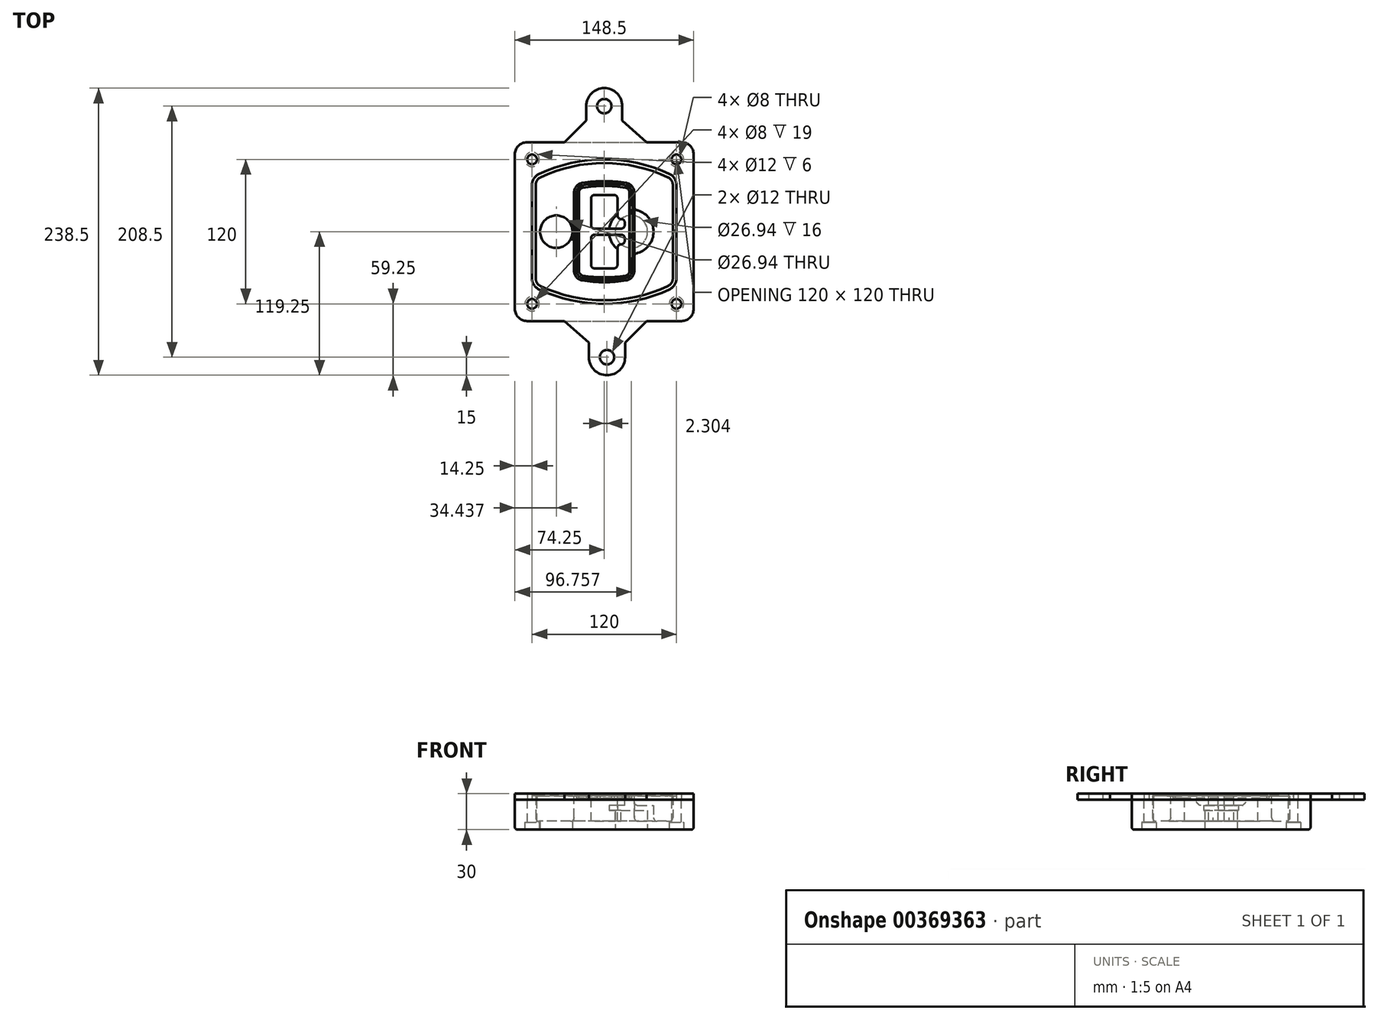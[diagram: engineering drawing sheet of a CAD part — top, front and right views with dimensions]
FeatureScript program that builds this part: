
annotation { "Feature Type Name" : "Feature", "Feature Type Description" : "" }
export const myFeature = defineFeature(function(context is Context, id is Id, definition is map)
    precondition{}
    {
        {
            var Q0;
            Q0=qCreatedBy(makeId("Top.planeOp"),FACE);
            var sketch = newSketch(context, id + "F0", { "sketchPlane" : qUnion([Q0])});
            skPoint(sketch, "E0.rect.middle", {"position": v(0, 0) * mm});
            skLineSegment(sketch, "E1.bottom", {"start": v(-64.25, -74.25) * mm, "end": v(64.25, -74.25) * mm});
            skLineSegment(sketch, "E1.top", {"start": v(-64.25, 74.25) * mm, "end": v(64.25, 74.25) * mm});
            skLineSegment(sketch, "E1.left", {"start": v(-74.25, -64.25) * mm, "end": v(-74.25, 64.25) * mm});
            skLineSegment(sketch, "E1.right", {"start": v(74.25, -64.25) * mm, "end": v(74.25, 64.25) * mm});
            skLineSegment(sketch, "E2", {"start": v(-74.25, 74.25) * mm, "end": v(74.25, -74.25) * mm, "construction": true});
            skLineSegment(sketch, "E3", {"start": v(74.25, 74.25) * mm, "end": v(-74.25, -74.25) * mm, "construction": true});
            skCircle(sketch, "E4", {"center": v(-60, 60) * mm, "radius": 4 * mm});
            skCircle(sketch, "E5", {"center": v(60, 60) * mm, "radius": 4 * mm});
            skCircle(sketch, "E6", {"center": v(60, -60) * mm, "radius": 4 * mm});
            skCircle(sketch, "E7", {"center": v(-60, -60) * mm, "radius": 4 * mm});
            skLineSegment(sketch, "E8", {"start": v(-60, 60) * mm, "end": v(60, 60) * mm, "construction": true});
            skLineSegment(sketch, "E9", {"start": v(60, 60) * mm, "end": v(60, -60) * mm, "construction": true});
            skLineSegment(sketch, "E10", {"start": v(60, -60) * mm, "end": v(-60, -60) * mm, "construction": true});
            skLineSegment(sketch, "E11", {"start": v(-60, -60) * mm, "end": v(-60, 60) * mm, "construction": true});
            skLineSegment(sketch, "E12", {"start": v(-60, 38.83) * mm, "end": v(-60, -38.83) * mm});
            skLineSegment(sketch, "E13", {"start": v(60, 38.83) * mm, "end": v(60, -38.83) * mm});
            skArc(sketch, "E14", {"start": v(54.26, 47.88) * mm, "mid": v(0, 60) * mm, "end": v(-54.26, 47.88) * mm});
            skArc(sketch, "E15", {"start": v(-54.26, -47.88) * mm, "mid": v(0, -60) * mm, "end": v(54.26, -47.88) * mm});
            skLineSegment(sketch, "E16", {"start": v(-60, 0) * mm, "end": v(60, 0) * mm, "construction": true});
            skPoint(sketch, "E17.visualSharp", {"position": v(-60, -45) * mm});
            skArc(sketch, "E17.filletArc", {"start": v(-60, -38.83) * mm, "mid": v(-58.44, -44.2) * mm, "end": v(-54.26, -47.88) * mm});
            skPoint(sketch, "E18.visualSharp", {"position": v(-60, 45) * mm});
            skArc(sketch, "E18.filletArc", {"start": v(-54.26, 47.88) * mm, "mid": v(-58.44, 44.2) * mm, "end": v(-60, 38.83) * mm});
            skPoint(sketch, "E19.visualSharp", {"position": v(60, 45) * mm});
            skArc(sketch, "E19.filletArc", {"start": v(60, 38.83) * mm, "mid": v(58.44, 44.2) * mm, "end": v(54.26, 47.88) * mm});
            skPoint(sketch, "E20.visualSharp", {"position": v(60, -45) * mm});
            skArc(sketch, "E20.filletArc", {"start": v(54.26, -47.88) * mm, "mid": v(58.44, -44.2) * mm, "end": v(60, -38.83) * mm});
            skPoint(sketch, "E21.visualSharp", {"position": v(-74.25, 74.25) * mm});
            skArc(sketch, "E21.filletArc", {"start": v(-64.25, 74.25) * mm, "mid": v(-71.32, 71.32) * mm, "end": v(-74.25, 64.25) * mm});
            skPoint(sketch, "E22.visualSharp", {"position": v(74.25, 74.25) * mm});
            skArc(sketch, "E22.filletArc", {"start": v(74.25, 64.25) * mm, "mid": v(71.32, 71.32) * mm, "end": v(64.25, 74.25) * mm});
            skPoint(sketch, "E23.visualSharp", {"position": v(74.25, -74.25) * mm});
            skArc(sketch, "E23.filletArc", {"start": v(64.25, -74.25) * mm, "mid": v(71.32, -71.32) * mm, "end": v(74.25, -64.25) * mm});
            skPoint(sketch, "E24.visualSharp", {"position": v(-74.25, -74.25) * mm});
            skArc(sketch, "E24.filletArc", {"start": v(-74.25, -64.25) * mm, "mid": v(-71.32, -71.32) * mm, "end": v(-64.25, -74.25) * mm});
            skArc(sketch, "E25.0", {"start": v(57, 38.83) * mm, "mid": v(55.9, 42.58) * mm, "end": v(52.98, 45.17) * mm});
            skLineSegment(sketch, "E25.1", {"start": v(57, 38.83) * mm, "end": v(57, -38.83) * mm});
            skArc(sketch, "E25.2", {"start": v(52.98, -45.17) * mm, "mid": v(55.9, -42.58) * mm, "end": v(57, -38.83) * mm});
            skArc(sketch, "E25.3", {"start": v(-52.98, -45.17) * mm, "mid": v(0, -57) * mm, "end": v(52.98, -45.17) * mm});
            skArc(sketch, "E25.4", {"start": v(-57, -38.83) * mm, "mid": v(-55.9, -42.58) * mm, "end": v(-52.98, -45.17) * mm});
            skArc(sketch, "E25.5", {"start": v(52.98, 45.17) * mm, "mid": v(0, 57) * mm, "end": v(-52.98, 45.17) * mm});
            skLineSegment(sketch, "E25.6", {"start": v(-57, 38.83) * mm, "end": v(-57, -38.83) * mm});
            skArc(sketch, "E25.7", {"start": v(-52.98, 45.17) * mm, "mid": v(-55.9, 42.58) * mm, "end": v(-57, 38.83) * mm});
            skArc(sketch, "E26.0", {"start": v(-55.96, 51.5) * mm, "mid": v(-61.82, 46.33) * mm, "end": v(-64, 38.83) * mm});
            skArc(sketch, "E26.1", {"start": v(55.96, 51.5) * mm, "mid": v(0, 64) * mm, "end": v(-55.96, 51.5) * mm});
            skArc(sketch, "E26.2", {"start": v(64, 38.83) * mm, "mid": v(61.82, 46.33) * mm, "end": v(55.96, 51.5) * mm});
            skLineSegment(sketch, "E26.3", {"start": v(64, 38.83) * mm, "end": v(64, -38.83) * mm});
            skArc(sketch, "E26.4", {"start": v(55.96, -51.5) * mm, "mid": v(61.82, -46.33) * mm, "end": v(64, -38.83) * mm});
            skLineSegment(sketch, "E26.5", {"start": v(-64, 38.83) * mm, "end": v(-64, -38.83) * mm});
            skArc(sketch, "E26.6", {"start": v(-55.96, -51.5) * mm, "mid": v(0, -64) * mm, "end": v(55.96, -51.5) * mm});
            skArc(sketch, "E26.7", {"start": v(-64, -38.83) * mm, "mid": v(-61.82, -46.33) * mm, "end": v(-55.96, -51.5) * mm});
            skSolve(sketch);
        }
        {
            var Q0;
            Q0=makeQuery(id+"F0.imprint","IMPRINT",FACE,{"disambiguationData":[TD([[makeQuery(id+"F0.imprint","IMPRINT",EDGE,{"derivedFrom":sQuery(id+"F0.wireOp",EDGE,"E1.bottom")}),1.0]])]});
            var Q1;
            Q1=makeQuery(id+"F0.imprint","IMPRINT",FACE,{"disambiguationData":[TD([[makeQuery(id+"F0.imprint","IMPRINT",EDGE,{"derivedFrom":sQuery(id+"F0.wireOp",EDGE,"E12")}),1.0]])]});
            var Q2;
            Q2=makeQuery(id+"F0.imprint","IMPRINT",FACE,{"disambiguationData":[TD([[makeQuery(id+"F0.imprint","IMPRINT",EDGE,{"derivedFrom":sQuery(id+"F0.wireOp",EDGE,"E25.0")}),1.0]])]});
            var Q3;
            Q3=makeQuery(id+"F0.imprint","IMPRINT",FACE,{"disambiguationData":[TD([[makeQuery(id+"F0.imprint","IMPRINT",EDGE,{"derivedFrom":sQuery(id+"F0.wireOp",EDGE,"E12")}),-1.0]])]});
            extrude(context, id + "F1", {"entities" : qUnion([Q0, Q1, Q2, Q3]), "oppositeDirection" : true, "depth" : 25 * mm});
        }
        {
            var Q0;
            Q0=makeQuery(id+"F0.imprint","IMPRINT",FACE,{"disambiguationData":[TD([[makeQuery(id+"F0.imprint","IMPRINT",EDGE,{"derivedFrom":sQuery(id+"F0.wireOp",EDGE,"E12")}),1.0]])]});
            extrude(context, id + "F2", {"entities" : qUnion([Q0]), "operationType" : NewBodyOperationType.ADD, "depth" : 3 * mm});
        }
        {
            var Q0;
            Q0=makeQuery(id+"F0.imprint","IMPRINT",FACE,{"disambiguationData":[TD([[makeQuery(id+"F0.imprint","IMPRINT",EDGE,{"derivedFrom":sQuery(id+"F0.wireOp",EDGE,"E25.0")}),1.0]])]});
            extrude(context, id + "F3", {"entities" : qUnion([Q0]), "operationType" : NewBodyOperationType.REMOVE, "oppositeDirection" : true, "depth" : 18 * mm});
        }
        {
            var Q0;
            Q0=makeQuery(id+"F2.opExtrude","CAP_FACE",FACE,{"disambiguationData":[OSD([sQuery(id+"F0.wireOp",EDGE,"E12"),sQuery(id+"F0.wireOp",EDGE,"E13"),sQuery(id+"F0.wireOp",EDGE,"E14"),sQuery(id+"F0.wireOp",EDGE,"E15"),sQuery(id+"F0.wireOp",EDGE,"E17.filletArc"),sQuery(id+"F0.wireOp",EDGE,"E18.filletArc"),sQuery(id+"F0.wireOp",EDGE,"E19.filletArc"),sQuery(id+"F0.wireOp",EDGE,"E20.filletArc"),sQuery(id+"F0.wireOp",EDGE,"E25.0"),sQuery(id+"F0.wireOp",EDGE,"E25.1"),sQuery(id+"F0.wireOp",EDGE,"E25.2"),sQuery(id+"F0.wireOp",EDGE,"E25.3"),sQuery(id+"F0.wireOp",EDGE,"E25.4"),sQuery(id+"F0.wireOp",EDGE,"E25.5"),sQuery(id+"F0.wireOp",EDGE,"E25.6"),sQuery(id+"F0.wireOp",EDGE,"E25.7")])],"isStart":false});
            var sketch = newSketch(context, id + "F4", { "sketchPlane" : qUnion([Q0])});
            skArc(sketch, "E27.0", {"start": v(-18.34, -40.45) * mm, "mid": v(0, -42) * mm, "end": v(18.34, -40.45) * mm});
            skArc(sketch, "E28.0", {"start": v(18.34, 40.45) * mm, "mid": v(0, 42) * mm, "end": v(-18.34, 40.45) * mm});
            skLineSegment(sketch, "E29", {"start": v(-25, 32.57) * mm, "end": v(-25, -32.57) * mm});
            skLineSegment(sketch, "E30", {"start": v(25, 32.57) * mm, "end": v(25, -32.57) * mm});
            skLineSegment(sketch, "E31", {"start": v(-25, 39.1) * mm, "end": v(25, 39.1) * mm, "construction": true});
            skLineSegment(sketch, "E32", {"start": v(-25, -39.1) * mm, "end": v(25, -39.1) * mm, "construction": true});
            skPoint(sketch, "E33.visualSharp", {"position": v(-25, 39.1) * mm});
            skArc(sketch, "E33.filletArc", {"start": v(-18.34, 40.45) * mm, "mid": v(-23.11, 37.73) * mm, "end": v(-25, 32.57) * mm});
            skPoint(sketch, "E34.visualSharp", {"position": v(25, 39.1) * mm});
            skArc(sketch, "E34.filletArc", {"start": v(25, 32.57) * mm, "mid": v(23.11, 37.73) * mm, "end": v(18.34, 40.45) * mm});
            skPoint(sketch, "E35.visualSharp", {"position": v(25, -39.1) * mm});
            skArc(sketch, "E35.filletArc", {"start": v(18.34, -40.45) * mm, "mid": v(23.11, -37.73) * mm, "end": v(25, -32.57) * mm});
            skPoint(sketch, "E36.visualSharp", {"position": v(-25, -39.1) * mm});
            skArc(sketch, "E36.filletArc", {"start": v(-25, -32.57) * mm, "mid": v(-23.11, -37.73) * mm, "end": v(-18.34, -40.45) * mm});
            skArc(sketch, "E37.0", {"start": v(52.98, 45.17) * mm, "mid": v(0, 57) * mm, "end": v(-52.98, 45.17) * mm});
            skArc(sketch, "E37.1", {"start": v(-52.98, 45.17) * mm, "mid": v(-55.9, 42.58) * mm, "end": v(-57, 38.83) * mm});
            skLineSegment(sketch, "E37.2", {"start": v(-57, 38.83) * mm, "end": v(-57, -38.83) * mm});
            skArc(sketch, "E37.3", {"start": v(-57, -38.83) * mm, "mid": v(-55.9, -42.58) * mm, "end": v(-52.98, -45.17) * mm});
            skArc(sketch, "E37.4", {"start": v(-52.98, -45.17) * mm, "mid": v(0, -57) * mm, "end": v(52.98, -45.17) * mm});
            skArc(sketch, "E37.5", {"start": v(52.98, -45.17) * mm, "mid": v(55.9, -42.58) * mm, "end": v(57, -38.83) * mm});
            skLineSegment(sketch, "E37.6", {"start": v(57, 38.83) * mm, "end": v(57, -38.83) * mm});
            skArc(sketch, "E37.7", {"start": v(57, 38.83) * mm, "mid": v(55.9, 42.58) * mm, "end": v(52.98, 45.17) * mm});
            skLineSegment(sketch, "E38.0", {"start": v(23, 32.57) * mm, "end": v(23, -32.57) * mm});
            skArc(sketch, "E38.1", {"start": v(18, -38.48) * mm, "mid": v(21.58, -36.44) * mm, "end": v(23, -32.57) * mm});
            skArc(sketch, "E38.2", {"start": v(-18, -38.48) * mm, "mid": v(0, -40) * mm, "end": v(18, -38.48) * mm});
            skArc(sketch, "E38.3", {"start": v(-23, -32.57) * mm, "mid": v(-21.58, -36.44) * mm, "end": v(-18, -38.48) * mm});
            skLineSegment(sketch, "E38.4", {"start": v(-23, 32.57) * mm, "end": v(-23, -32.57) * mm});
            skArc(sketch, "E38.5", {"start": v(23, 32.57) * mm, "mid": v(21.58, 36.44) * mm, "end": v(18, 38.48) * mm});
            skArc(sketch, "E38.6", {"start": v(-18, 38.48) * mm, "mid": v(-21.58, 36.44) * mm, "end": v(-23, 32.57) * mm});
            skArc(sketch, "E38.7", {"start": v(18, 38.48) * mm, "mid": v(0, 40) * mm, "end": v(-18, 38.48) * mm});
            skArc(sketch, "E39.0", {"start": v(21, 32.57) * mm, "mid": v(20.06, 35.15) * mm, "end": v(17.67, 36.5) * mm});
            skLineSegment(sketch, "E39.1", {"start": v(21, 32.57) * mm, "end": v(21, -32.57) * mm});
            skArc(sketch, "E39.2", {"start": v(17.67, -36.5) * mm, "mid": v(20.06, -35.15) * mm, "end": v(21, -32.57) * mm});
            skArc(sketch, "E39.3", {"start": v(-17.67, -36.5) * mm, "mid": v(0, -38) * mm, "end": v(17.67, -36.5) * mm});
            skArc(sketch, "E39.4", {"start": v(-21, -32.57) * mm, "mid": v(-20.06, -35.15) * mm, "end": v(-17.67, -36.5) * mm});
            skArc(sketch, "E39.5", {"start": v(17.67, 36.5) * mm, "mid": v(0, 38) * mm, "end": v(-17.67, 36.5) * mm});
            skLineSegment(sketch, "E39.6", {"start": v(-21, 32.57) * mm, "end": v(-21, -32.57) * mm});
            skArc(sketch, "E39.7", {"start": v(-17.67, 36.5) * mm, "mid": v(-20.06, 35.15) * mm, "end": v(-21, 32.57) * mm});
            skLineSegment(sketch, "E40", {"start": v(-25, 0) * mm, "end": v(25, 0) * mm, "construction": true});
            skLineSegment(sketch, "E41", {"start": v(-11, 5.5) * mm, "end": v(-11, 27.5) * mm});
            skLineSegment(sketch, "E42", {"start": v(-8, 30.5) * mm, "end": v(8, 30.5) * mm});
            skLineSegment(sketch, "E43", {"start": v(11, 27.5) * mm, "end": v(11, 13.5) * mm});
            skLineSegment(sketch, "E44", {"start": v(14, 10.5) * mm, "end": v(14, 10.5) * mm});
            skLineSegment(sketch, "E45", {"start": v(17, 7.5) * mm, "end": v(17, 5.5) * mm});
            skLineSegment(sketch, "E46", {"start": v(14, 2.5) * mm, "end": v(-8, 2.5) * mm});
            skPoint(sketch, "E47.visualSharp", {"position": v(-11, 30.5) * mm});
            skArc(sketch, "E47.filletArc", {"start": v(-8, 30.5) * mm, "mid": v(-10.12, 29.62) * mm, "end": v(-11, 27.5) * mm});
            skPoint(sketch, "E48.visualSharp", {"position": v(11, 30.5) * mm});
            skArc(sketch, "E48.filletArc", {"start": v(11, 27.5) * mm, "mid": v(10.12, 29.62) * mm, "end": v(8, 30.5) * mm});
            skPoint(sketch, "E49.visualSharp", {"position": v(11, 10.5) * mm});
            skArc(sketch, "E49.filletArc", {"start": v(11, 13.5) * mm, "mid": v(11.88, 11.38) * mm, "end": v(14, 10.5) * mm});
            skPoint(sketch, "E50.visualSharp", {"position": v(17, 10.5) * mm});
            skArc(sketch, "E50.filletArc", {"start": v(17, 7.5) * mm, "mid": v(16.12, 9.62) * mm, "end": v(14, 10.5) * mm});
            skPoint(sketch, "E51.visualSharp", {"position": v(17, 2.5) * mm});
            skArc(sketch, "E51.filletArc", {"start": v(14, 2.5) * mm, "mid": v(16.12, 3.38) * mm, "end": v(17, 5.5) * mm});
            skPoint(sketch, "E52.visualSharp", {"position": v(-11, 2.5) * mm});
            skArc(sketch, "E52.filletArc", {"start": v(-11, 5.5) * mm, "mid": v(-10.12, 3.38) * mm, "end": v(-8, 2.5) * mm});
            skLineSegment(sketch, "E53.0.MirrorCS", {"start": v(14, -2.5) * mm, "end": v(-8, -2.5) * mm});
            skArc(sketch, "E54.0.MirrorCS", {"start": v(-11, -5.5) * mm, "mid": v(-10.12, -3.38) * mm, "end": v(-8, -2.5) * mm});
            skLineSegment(sketch, "E55.0.MirrorCS", {"start": v(-11, -5.5) * mm, "end": v(-11, -27.5) * mm});
            skArc(sketch, "E56.0.MirrorCS", {"start": v(-8, -30.5) * mm, "mid": v(-10.12, -29.62) * mm, "end": v(-11, -27.5) * mm});
            skLineSegment(sketch, "E57.0.MirrorCS", {"start": v(-8, -30.5) * mm, "end": v(8, -30.5) * mm});
            skArc(sketch, "E58.0.MirrorCS", {"start": v(11, -27.5) * mm, "mid": v(10.12, -29.62) * mm, "end": v(8, -30.5) * mm});
            skLineSegment(sketch, "E59.0.MirrorCS", {"start": v(11, -27.5) * mm, "end": v(11, -13.5) * mm});
            skArc(sketch, "E60.0.MirrorCS", {"start": v(11, -13.5) * mm, "mid": v(11.88, -11.38) * mm, "end": v(14, -10.5) * mm});
            skArc(sketch, "E61.0.MirrorCS", {"start": v(17, -7.5) * mm, "mid": v(16.12, -9.62) * mm, "end": v(14, -10.5) * mm});
            skLineSegment(sketch, "E62.0.MirrorCS", {"start": v(17, -7.5) * mm, "end": v(17, -5.5) * mm});
            skArc(sketch, "E63.0.MirrorCS", {"start": v(14, -2.5) * mm, "mid": v(16.12, -3.38) * mm, "end": v(17, -5.5) * mm});
            skSolve(sketch);
        }
        {
            var Q0;
            Q0=makeQuery(id+"F4.imprint","IMPRINT",FACE,{"disambiguationData":[TD([[makeQuery(id+"F4.imprint","IMPRINT",EDGE,{"derivedFrom":sQuery(id+"F4.wireOp",EDGE,"E27.0")}),1.0]])]});
            var Q1;
            Q1=makeQuery(id+"F4.imprint","IMPRINT",FACE,{"disambiguationData":[TD([[makeQuery(id+"F4.imprint","IMPRINT",EDGE,{"derivedFrom":sQuery(id+"F4.wireOp",EDGE,"E38.0")}),-1.0]])]});
            var Q2;
            Q2=makeQuery(id+"F4.imprint","IMPRINT",FACE,{"disambiguationData":[TD([[makeQuery(id+"F4.imprint","IMPRINT",EDGE,{"derivedFrom":sQuery(id+"F4.wireOp",EDGE,"E39.0")}),1.0]])]});
            extrude(context, id + "F5", {"entities" : qUnion([Q0, Q1, Q2]), "operationType" : NewBodyOperationType.ADD, "endBound" : BoundingType.UP_TO_NEXT, "oppositeDirection" : true, "depth" : 25 * mm});
        }
        {
            var Q0;
            Q0=makeQuery(id+"F4.imprint","IMPRINT",FACE,{"disambiguationData":[TD([[makeQuery(id+"F4.imprint","IMPRINT",EDGE,{"derivedFrom":sQuery(id+"F4.wireOp",EDGE,"E38.0")}),-1.0]])]});
            extrude(context, id + "F6", {"entities" : qUnion([Q0]), "operationType" : NewBodyOperationType.REMOVE, "oppositeDirection" : true, "depth" : 2 * mm});
        }
        {
            var Q0;
            Q0=makeQuery(id+"F1.opExtrude","CAP_FACE",FACE,{"disambiguationData":[OSD([sQuery(id+"F0.wireOp",EDGE,"E1.bottom"),sQuery(id+"F0.wireOp",EDGE,"E1.top"),sQuery(id+"F0.wireOp",EDGE,"E1.left"),sQuery(id+"F0.wireOp",EDGE,"E1.right"),sQuery(id+"F0.wireOp",EDGE,"E4"),sQuery(id+"F0.wireOp",EDGE,"E5"),sQuery(id+"F0.wireOp",EDGE,"E6"),sQuery(id+"F0.wireOp",EDGE,"E7"),sQuery(id+"F0.wireOp",EDGE,"E21.filletArc"),sQuery(id+"F0.wireOp",EDGE,"E22.filletArc"),sQuery(id+"F0.wireOp",EDGE,"E23.filletArc"),sQuery(id+"F0.wireOp",EDGE,"E24.filletArc")])],"isStart":false});
            var sketch = newSketch(context, id + "F7", { "sketchPlane" : qUnion([Q0])});
            skCircle(sketch, "E64", {"center": v(22.5, 0) * mm, "radius": 13.47 * mm});
            skCircle(sketch, "E65", {"center": v(-39.81, 0) * mm, "radius": 13.47 * mm});
            skLineSegment(sketch, "E66", {"start": v(74.25, 0) * mm, "end": v(-74.25, 0) * mm});
            skCircle(sketch, "E67", {"center": v(22.5, 0) * mm, "radius": 18.47 * mm});
            skCircle(sketch, "E68", {"center": v(60, -60) * mm, "radius": 6 * mm});
            skCircle(sketch, "E69", {"center": v(-60, -60) * mm, "radius": 6 * mm});
            skCircle(sketch, "E70", {"center": v(-60, 60) * mm, "radius": 6 * mm});
            skCircle(sketch, "E71", {"center": v(60, 60) * mm, "radius": 6 * mm});
            skSolve(sketch);
        }
        {
            var Q0;
            {var subQ1=sQuery(id+"F7.wireOp",EDGE,"E66");var subQ4=sQuery(id+"F7.wireOp",EDGE,"E64");var subQ6=makeQuery(id+"F7.imprint","INTERSECT",VERTEX,{"disambiguationData":[OD(0.0)],"derivedFrom":[subQ4,subQ1]});Q0=makeQuery(id+"F7.imprint","IMPRINT",FACE,{"disambiguationData":[TD([[makeQuery(id+"F7.imprint","IMPRINT",EDGE,{"disambiguationData":[TD([[subQ6,-1.0]])],"derivedFrom":subQ4}),-1.0]])]});}
            var Q1;
            {var subQ0=sQuery(id+"F7.wireOp",EDGE,"E66");var subQ1=sQuery(id+"F7.wireOp",EDGE,"E64");var subQ3=makeQuery(id+"F7.imprint","INTERSECT",VERTEX,{"disambiguationData":[OD(0.0)],"derivedFrom":[subQ1,subQ0]});Q1=makeQuery(id+"F7.imprint","IMPRINT",FACE,{"disambiguationData":[TD([[makeQuery(id+"F7.imprint","IMPRINT",EDGE,{"disambiguationData":[TD([[subQ3,-1.0]])],"derivedFrom":subQ1}),1.0]])]});}
            var Q2;
            {var subQ0=sQuery(id+"F7.wireOp",EDGE,"E66");var subQ1=sQuery(id+"F7.wireOp",EDGE,"E64");var subQ3=makeQuery(id+"F7.imprint","INTERSECT",VERTEX,{"disambiguationData":[OD(0.0)],"derivedFrom":[subQ1,subQ0]});Q2=makeQuery(id+"F7.imprint","IMPRINT",FACE,{"disambiguationData":[TD([[makeQuery(id+"F7.imprint","IMPRINT",EDGE,{"disambiguationData":[TD([[subQ3,1.0]])],"derivedFrom":subQ1}),1.0]])]});}
            var Q3;
            {var subQ1=sQuery(id+"F7.wireOp",EDGE,"E66");var subQ4=sQuery(id+"F7.wireOp",EDGE,"E64");var subQ6=makeQuery(id+"F7.imprint","INTERSECT",VERTEX,{"disambiguationData":[OD(0.0)],"derivedFrom":[subQ4,subQ1]});Q3=makeQuery(id+"F7.imprint","IMPRINT",FACE,{"disambiguationData":[TD([[makeQuery(id+"F7.imprint","IMPRINT",EDGE,{"disambiguationData":[TD([[subQ6,1.0]])],"derivedFrom":subQ4}),-1.0]])]});}
            extrude(context, id + "F8", {"entities" : qUnion([Q0, Q1, Q2, Q3]), "operationType" : NewBodyOperationType.ADD, "oppositeDirection" : true, "depth" : 20 * mm});
        }
        {
            var Q0;
            {var subQ0=sQuery(id+"F7.wireOp",EDGE,"E66");var subQ1=sQuery(id+"F7.wireOp",EDGE,"E64");var subQ3=makeQuery(id+"F7.imprint","INTERSECT",VERTEX,{"disambiguationData":[OD(0.0)],"derivedFrom":[subQ1,subQ0]});Q0=makeQuery(id+"F7.imprint","IMPRINT",FACE,{"disambiguationData":[TD([[makeQuery(id+"F7.imprint","IMPRINT",EDGE,{"disambiguationData":[TD([[subQ3,-1.0]])],"derivedFrom":subQ1}),1.0]])]});}
            var Q1;
            {var subQ0=sQuery(id+"F7.wireOp",EDGE,"E66");var subQ1=sQuery(id+"F7.wireOp",EDGE,"E64");var subQ3=makeQuery(id+"F7.imprint","INTERSECT",VERTEX,{"disambiguationData":[OD(0.0)],"derivedFrom":[subQ1,subQ0]});Q1=makeQuery(id+"F7.imprint","IMPRINT",FACE,{"disambiguationData":[TD([[makeQuery(id+"F7.imprint","IMPRINT",EDGE,{"disambiguationData":[TD([[subQ3,1.0]])],"derivedFrom":subQ1}),1.0]])]});}
            extrude(context, id + "F9", {"entities" : qUnion([Q0, Q1]), "operationType" : NewBodyOperationType.REMOVE, "oppositeDirection" : true, "depth" : 16 * mm});
        }
        {
            var Q0;
            {var subQ0=sQuery(id+"F7.wireOp",EDGE,"E66");var subQ1=sQuery(id+"F7.wireOp",EDGE,"E65");var subQ3=makeQuery(id+"F7.imprint","INTERSECT",VERTEX,{"disambiguationData":[OD(0.0)],"derivedFrom":[subQ1,subQ0]});Q0=makeQuery(id+"F7.imprint","IMPRINT",FACE,{"disambiguationData":[TD([[makeQuery(id+"F7.imprint","IMPRINT",EDGE,{"disambiguationData":[TD([[subQ3,-1.0]])],"derivedFrom":subQ1}),1.0]])]});}
            var Q1;
            {var subQ0=sQuery(id+"F7.wireOp",EDGE,"E66");var subQ1=sQuery(id+"F7.wireOp",EDGE,"E65");var subQ3=makeQuery(id+"F7.imprint","INTERSECT",VERTEX,{"disambiguationData":[OD(0.0)],"derivedFrom":[subQ1,subQ0]});Q1=makeQuery(id+"F7.imprint","IMPRINT",FACE,{"disambiguationData":[TD([[makeQuery(id+"F7.imprint","IMPRINT",EDGE,{"disambiguationData":[TD([[subQ3,1.0]])],"derivedFrom":subQ1}),1.0]])]});}
            extrude(context, id + "F10", {"entities" : qUnion([Q0, Q1]), "operationType" : NewBodyOperationType.REMOVE, "oppositeDirection" : true, "depth" : 25 * mm});
        }
        {
            var Q0;
            Q0=makeQuery(id+"F7.imprint","IMPRINT",FACE,{"disambiguationData":[TD([[makeQuery(id+"F7.imprint","IMPRINT",EDGE,{"derivedFrom":sQuery(id+"F7.wireOp",EDGE,"E68")}),1.0]])]});
            var Q1;
            Q1=makeQuery(id+"F7.imprint","IMPRINT",FACE,{"disambiguationData":[TD([[makeQuery(id+"F7.imprint","IMPRINT",EDGE,{"derivedFrom":makeQuery(id+"F1.opExtrude","CAP_EDGE",EDGE,{"disambiguationData":[OSD([sQuery(id+"F0.wireOp",EDGE,"E5")])],"isStart":false})}),-1.0]])]});
            var Q2;
            Q2=makeQuery(id+"F7.imprint","IMPRINT",FACE,{"disambiguationData":[TD([[makeQuery(id+"F7.imprint","IMPRINT",EDGE,{"derivedFrom":sQuery(id+"F7.wireOp",EDGE,"E69")}),1.0]])]});
            var Q3;
            Q3=makeQuery(id+"F7.imprint","IMPRINT",FACE,{"disambiguationData":[TD([[makeQuery(id+"F7.imprint","IMPRINT",EDGE,{"derivedFrom":makeQuery(id+"F1.opExtrude","CAP_EDGE",EDGE,{"disambiguationData":[OSD([sQuery(id+"F0.wireOp",EDGE,"E4")])],"isStart":false})}),-1.0]])]});
            var Q4;
            Q4=makeQuery(id+"F7.imprint","IMPRINT",FACE,{"disambiguationData":[TD([[makeQuery(id+"F7.imprint","IMPRINT",EDGE,{"derivedFrom":sQuery(id+"F7.wireOp",EDGE,"E70")}),1.0]])]});
            var Q5;
            Q5=makeQuery(id+"F7.imprint","IMPRINT",FACE,{"disambiguationData":[TD([[makeQuery(id+"F7.imprint","IMPRINT",EDGE,{"derivedFrom":makeQuery(id+"F1.opExtrude","CAP_EDGE",EDGE,{"disambiguationData":[OSD([sQuery(id+"F0.wireOp",EDGE,"E7")])],"isStart":false})}),-1.0]])]});
            var Q6;
            Q6=makeQuery(id+"F7.imprint","IMPRINT",FACE,{"disambiguationData":[TD([[makeQuery(id+"F7.imprint","IMPRINT",EDGE,{"derivedFrom":sQuery(id+"F7.wireOp",EDGE,"E71")}),1.0]])]});
            var Q7;
            Q7=makeQuery(id+"F7.imprint","IMPRINT",FACE,{"disambiguationData":[TD([[makeQuery(id+"F7.imprint","IMPRINT",EDGE,{"derivedFrom":makeQuery(id+"F1.opExtrude","CAP_EDGE",EDGE,{"disambiguationData":[OSD([sQuery(id+"F0.wireOp",EDGE,"E6")])],"isStart":false})}),-1.0]])]});
            extrude(context, id + "F11", {"entities" : qUnion([Q0, Q1, Q2, Q3, Q4, Q5, Q6, Q7]), "operationType" : NewBodyOperationType.REMOVE, "oppositeDirection" : true, "depth" : 6 * mm});
        }
        {
            var Q0;
            Q0=makeQuery(id+"F9.boolean.opBoolean","COPY",FACE,{"derivedFrom":makeQuery(id+"F9.opExtrude","CAP_FACE",FACE,{"disambiguationData":[OSD([sQuery(id+"F7.wireOp",EDGE,"E64")])],"isStart":false})});
            var sketch = newSketch(context, id + "F12", { "sketchPlane" : qUnion([Q0])});
            skArc(sketch, "E72.0", {"start": v(11, 14.45) * mm, "mid": v(6.45, 9.13) * mm, "end": v(4.2, 2.5) * mm});
            skArc(sketch, "E72.1", {"start": v(4.2, -2.5) * mm, "mid": v(6.45, -9.13) * mm, "end": v(11, -14.45) * mm});
            skLineSegment(sketch, "E73", {"start": v(4.2, -2.5) * mm, "end": v(14, -2.5) * mm});
            skLineSegment(sketch, "E74.0", {"start": v(14, 2.5) * mm, "end": v(4.2, 2.5) * mm});
            skArc(sketch, "E74.1", {"start": v(14, 2.5) * mm, "mid": v(16.12, 3.38) * mm, "end": v(17, 5.5) * mm});
            skLineSegment(sketch, "E74.2", {"start": v(17, 7.5) * mm, "end": v(17, 5.5) * mm});
            skArc(sketch, "E74.3", {"start": v(17, 7.5) * mm, "mid": v(16.12, 9.62) * mm, "end": v(14, 10.5) * mm});
            skArc(sketch, "E74.4", {"start": v(11, 13.5) * mm, "mid": v(11.88, 11.38) * mm, "end": v(14, 10.5) * mm});
            skLineSegment(sketch, "E74.5", {"start": v(11, 14.45) * mm, "end": v(11, 13.5) * mm});
            skLineSegment(sketch, "E74.7", {"start": v(14, -2.5) * mm, "end": v(4.2, -2.5) * mm});
            skArc(sketch, "E74.8", {"start": v(14, -2.5) * mm, "mid": v(16.12, -3.38) * mm, "end": v(17, -5.5) * mm});
            skLineSegment(sketch, "E74.9", {"start": v(17, -7.5) * mm, "end": v(17, -5.5) * mm});
            skArc(sketch, "E74.10", {"start": v(17, -7.5) * mm, "mid": v(16.12, -9.62) * mm, "end": v(14, -10.5) * mm});
            skArc(sketch, "E74.11", {"start": v(11, -13.5) * mm, "mid": v(11.88, -11.38) * mm, "end": v(14, -10.5) * mm});
            skLineSegment(sketch, "E74.12", {"start": v(11, -14.45) * mm, "end": v(11, -13.5) * mm});
            skPoint(sketch, "E75.orphan", {"position": v(11, -27.5) * mm});
            skPoint(sketch, "E76.orphan", {"position": v(-8, -2.5) * mm});
            skPoint(sketch, "E77.orphan", {"position": v(-8, 2.5) * mm});
            skPoint(sketch, "E78.orphan", {"position": v(11, 27.5) * mm});
            skSolve(sketch);
        }
        {
            var Q0;
            {var subQ7=sQuery(id+"F12.wireOp",EDGE,"E72.0");var subQ14=sQuery(id+"F12.wireOp",EDGE,"E72.1");var subQ16=sQuery(id+"F12.wireOp",EDGE,"E74.1");var subQ18=sQuery(id+"F12.wireOp",EDGE,"E74.8");Q0=qUnion([makeQuery(id+"F12.imprint","IMPRINT",FACE,{"disambiguationData":[TD([[makeQuery(id+"F12.imprint","IMPRINT",EDGE,{"derivedFrom":subQ7}),1.0]])]}),makeQuery(id+"F12.imprint","IMPRINT",FACE,{"disambiguationData":[TD([[makeQuery(id+"F12.imprint","IMPRINT",EDGE,{"derivedFrom":subQ14}),1.0]])]}),makeQuery(id+"F12.imprint","IMPRINT",FACE,{"disambiguationData":[TD([[makeQuery(id+"F12.imprint","IMPRINT",EDGE,{"derivedFrom":subQ16}),1.0]])]}),makeQuery(id+"F12.imprint","IMPRINT",FACE,{"disambiguationData":[TD([[makeQuery(id+"F12.imprint","IMPRINT",EDGE,{"derivedFrom":subQ18}),-1.0]])]})]);}
            var Q1;
            Q1=makeQuery(id+"F5.boolean.opBoolean","SPLIT",FACE,{"disambiguationData":[TD([makeQuery(id+"F5.opExtrude","SWEPT_FACE",FACE,{"disambiguationData":[OSD([sQuery(id+"F4.wireOp",EDGE,"E41")])]})])],"derivedFrom":makeQuery(id+"F3.boolean.opBoolean","COPY",FACE,{"derivedFrom":makeQuery(id+"F3.opExtrude","CAP_FACE",FACE,{"disambiguationData":[OSD([sQuery(id+"F0.wireOp",EDGE,"E25.0"),sQuery(id+"F0.wireOp",EDGE,"E25.1"),sQuery(id+"F0.wireOp",EDGE,"E25.2"),sQuery(id+"F0.wireOp",EDGE,"E25.3"),sQuery(id+"F0.wireOp",EDGE,"E25.4"),sQuery(id+"F0.wireOp",EDGE,"E25.5"),sQuery(id+"F0.wireOp",EDGE,"E25.6"),sQuery(id+"F0.wireOp",EDGE,"E25.7")])],"isStart":false})})});
            extrude(context, id + "F13", {"entities" : qUnion([Q0]), "operationType" : NewBodyOperationType.REMOVE, "endBound" : BoundingType.UP_TO_SURFACE, "endBoundEntityFace" : qUnion([Q1]), "depth" : 25 * mm});
        }
        {
            var Q0;
            Q0=makeQuery(id+"F3.boolean.opBoolean","COPY",EDGE,{"derivedFrom":makeQuery(id+"F3.opExtrude","CAP_EDGE",EDGE,{"disambiguationData":[OSD([sQuery(id+"F0.wireOp",EDGE,"E25.6")])],"isStart":false})});
            var Q1;
            Q1=makeQuery(id+"F8.boolean.opBoolean","INTERSECT",EDGE,{"derivedFrom":[makeQuery(id+"F5.opExtrude","SWEPT_FACE",FACE,{"disambiguationData":[OSD([sQuery(id+"F4.wireOp",EDGE,"E30")])]}),makeQuery(id+"F8.opExtrude","CAP_FACE",FACE,{"disambiguationData":[OSD([sQuery(id+"F7.wireOp",EDGE,"E67")])],"isStart":false})]});
            var Q2;
            Q2=makeQuery(id+"F8.boolean.opBoolean","INTERSECT",EDGE,{"disambiguationData":[OD(1.0)],"derivedFrom":[makeQuery(id+"F5.opExtrude","SWEPT_FACE",FACE,{"disambiguationData":[OSD([sQuery(id+"F4.wireOp",EDGE,"E30")])]}),makeQuery(id+"F8.opExtrude","SWEPT_FACE",FACE,{"disambiguationData":[OSD([sQuery(id+"F7.wireOp",EDGE,"E67")])]})]});
            var Q3;
            {var subQ0=sQuery(id+"F4.wireOp",EDGE,"E30");Q3=makeQuery(id+"F8.boolean.opBoolean","SPLIT",EDGE,{"disambiguationData":[TD([makeQuery(id+"F5.opExtrude","SWEPT_FACE",FACE,{"disambiguationData":[OSD([sQuery(id+"F4.wireOp",EDGE,"E35.filletArc")])]})])],"derivedFrom":makeQuery(id+"F5.opExtrude","CAP_EDGE",EDGE,{"disambiguationData":[OSD([subQ0])],"isStart":false})});}
            var Q4;
            {var subQ0=sQuery(id+"F0.wireOp",EDGE,"E25.7");var subQ1=sQuery(id+"F0.wireOp",EDGE,"E25.1");var subQ2=sQuery(id+"F0.wireOp",EDGE,"E25.6");var subQ3=sQuery(id+"F0.wireOp",EDGE,"E25.5");var subQ4=sQuery(id+"F0.wireOp",EDGE,"E25.4");var subQ5=sQuery(id+"F0.wireOp",EDGE,"E25.0");var subQ6=sQuery(id+"F0.wireOp",EDGE,"E25.2");var subQ7=sQuery(id+"F0.wireOp",EDGE,"E25.3");Q4=makeQuery(id+"F8.boolean.opBoolean","INTERSECT",EDGE,{"derivedFrom":[makeQuery(id+"F5.boolean.opBoolean","SPLIT",FACE,{"disambiguationData":[TD([makeQuery(id+"F2.opExtrude","SWEPT_FACE",FACE,{"disambiguationData":[OSD([subQ5])]})])],"derivedFrom":makeQuery(id+"F3.boolean.opBoolean","COPY",FACE,{"derivedFrom":makeQuery(id+"F3.opExtrude","CAP_FACE",FACE,{"disambiguationData":[OSD([subQ5,subQ1,subQ6,subQ7,subQ4,subQ3,subQ2,subQ0])],"isStart":false})})}),makeQuery(id+"F8.opExtrude","SWEPT_FACE",FACE,{"disambiguationData":[OSD([sQuery(id+"F7.wireOp",EDGE,"E67")])]})]});}
            var Q5;
            Q5=makeQuery(id+"F8.boolean.opBoolean","INTERSECT",EDGE,{"disambiguationData":[OD(0.0)],"derivedFrom":[makeQuery(id+"F5.opExtrude","SWEPT_FACE",FACE,{"disambiguationData":[OSD([sQuery(id+"F4.wireOp",EDGE,"E30")])]}),makeQuery(id+"F8.opExtrude","SWEPT_FACE",FACE,{"disambiguationData":[OSD([sQuery(id+"F7.wireOp",EDGE,"E67")])]})]});
            fillet(context, id + "F14", {"entities" : qUnion([Q0, Q1, Q2, Q3, Q4, Q5]), "radius" : 3 * mm, "tangentPropagation" : true, "allowEdgeOverflow" : false});
        }
        {
            var Q0;
            Q0=makeQuery(id+"F1.opExtrude","CAP_EDGE",EDGE,{"disambiguationData":[OSD([sQuery(id+"F0.wireOp",EDGE,"E1.bottom")])],"isStart":false});
            fillet(context, id + "F15", {"entities" : qUnion([Q0]), "radius" : 2 * mm, "tangentPropagation" : true, "allowEdgeOverflow" : false});
        }
        {
            var Q0;
            {var subQ0=sQuery(id+"F0.wireOp",EDGE,"E21.filletArc");var subQ1=sQuery(id+"F0.wireOp",EDGE,"E7");var subQ2=sQuery(id+"F0.wireOp",EDGE,"E6");var subQ3=sQuery(id+"F0.wireOp",EDGE,"E5");var subQ4=sQuery(id+"F0.wireOp",EDGE,"E4");var subQ5=sQuery(id+"F0.wireOp",EDGE,"E22.filletArc");var subQ6=sQuery(id+"F0.wireOp",EDGE,"E1.bottom");var subQ7=sQuery(id+"F0.wireOp",EDGE,"E1.right");var subQ8=sQuery(id+"F0.wireOp",EDGE,"E1.top");var subQ9=sQuery(id+"F0.wireOp",EDGE,"E1.left");var subQ10=sQuery(id+"F0.wireOp",EDGE,"E23.filletArc");var subQ11=sQuery(id+"F0.wireOp",EDGE,"E24.filletArc");Q0=makeQuery(id+"F2.boolean.opBoolean","SPLIT",FACE,{"disambiguationData":[TD([makeQuery(id+"F1.opExtrude","SWEPT_FACE",FACE,{"disambiguationData":[OSD([subQ6])]})])],"derivedFrom":makeQuery(id+"F1.opExtrude","CAP_FACE",FACE,{"disambiguationData":[OSD([subQ6,subQ8,subQ9,subQ7,subQ4,subQ3,subQ2,subQ1,subQ0,subQ5,subQ10,subQ11])],"isStart":true})});}
            var sketch = newSketch(context, id + "F16", { "sketchPlane" : qUnion([Q0])});
            skLineSegment(sketch, "E79", {"start": v(0, 74.25) * mm, "end": v(0, 104.25) * mm, "construction": true});
            skCircle(sketch, "E80", {"center": v(0, 104.25) * mm, "radius": 6 * mm});
            skArc(sketch, "E81", {"start": v(0, 119.25) * mm, "mid": v(10.6, 114.86) * mm, "end": v(15, 104.25) * mm});
            skArc(sketch, "E82", {"start": v(0, 119.25) * mm, "mid": v(-10.6, 114.86) * mm, "end": v(-15, 104.25) * mm});
            skLineSegment(sketch, "E83", {"start": v(-15, 104.25) * mm, "end": v(-15, 92.25) * mm});
            skLineSegment(sketch, "E84", {"start": v(15, 104.25) * mm, "end": v(15, 92.25) * mm});
            skLineSegment(sketch, "E85", {"start": v(-15, 92.25) * mm, "end": v(-33, 74.25) * mm});
            skLineSegment(sketch, "E86", {"start": v(15, 92.25) * mm, "end": v(35.3, 74.25) * mm});
            skLineSegment(sketch, "E87", {"start": v(2.3, -74.25) * mm, "end": v(2.3, -104.25) * mm, "construction": true});
            skCircle(sketch, "E88", {"center": v(2.3, -104.25) * mm, "radius": 6 * mm});
            skArc(sketch, "E89", {"start": v(2.3, -119.25) * mm, "mid": v(-8.3, -114.86) * mm, "end": v(-12.7, -104.25) * mm});
            skArc(sketch, "E90", {"start": v(2.3, -119.25) * mm, "mid": v(12.91, -114.86) * mm, "end": v(17.3, -104.25) * mm});
            skLineSegment(sketch, "E91", {"start": v(17.3, -104.25) * mm, "end": v(17.3, -92.25) * mm});
            skLineSegment(sketch, "E92", {"start": v(-12.7, -104.25) * mm, "end": v(-12.7, -92.25) * mm});
            skLineSegment(sketch, "E93", {"start": v(17.3, -92.25) * mm, "end": v(35.3, -74.25) * mm});
            skLineSegment(sketch, "E94", {"start": v(-12.7, -92.25) * mm, "end": v(-33, -74.25) * mm});
            skSolve(sketch);
        }
        {
            var Q0;
            Q0=makeQuery(id+"F16.imprint","IMPRINT",FACE,{"disambiguationData":[TD([[makeQuery(id+"F16.imprint","IMPRINT",EDGE,{"derivedFrom":sQuery(id+"F16.wireOp",EDGE,"E80")}),-1.0]])]});
            var Q1;
            Q1=makeQuery(id+"F16.imprint","IMPRINT",FACE,{"disambiguationData":[TD([[makeQuery(id+"F16.imprint","IMPRINT",EDGE,{"derivedFrom":sQuery(id+"F16.wireOp",EDGE,"E88")}),-1.0]])]});
            var Q2;
            Q2=makeQuery(id+"F16.imprint","IMPRINT",FACE,{"disambiguationData":[TD([[makeQuery(id+"F16.imprint","IMPRINT",EDGE,{"derivedFrom":makeQuery(id+"F1.opExtrude","CAP_EDGE",EDGE,{"disambiguationData":[OSD([sQuery(id+"F0.wireOp",EDGE,"E1.left")])],"isStart":true})}),-1.0]])]});
            extrude(context, id + "F17", {"entities" : qUnion([Q0, Q1, Q2]), "depth" : 5 * mm});
        }
    });
